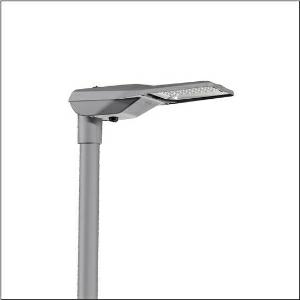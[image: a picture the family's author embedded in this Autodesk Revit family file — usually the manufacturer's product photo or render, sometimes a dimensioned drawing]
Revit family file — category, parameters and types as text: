
# Revit family: streetlight_sl_21_mini___p0_8ab_5xe2r33t08jb_257d
name_source: partatom
category: Lighting Fixtures
units: mm (PartAtom-declared; Revit-internal decimal feet)

## family parameters
Cut with Voids When Loaded = No
Host = Face
Light Source = No
Part Type = Normal
Room Calculation Point = No
Round Connector Dimension = Use Diameter
Shared = No

## types (1)
- --- (1 x LED, 11230 lm, 88.6 W, 3000K)
    Apparent Load = 89 VA
    CIE Flux Codes = 39 72 97 100 100
    Color Rendering = 70
    Color Temperature = 3000K
    Default Elevation = 1800 mm
    Description = Streetlight SL 21 mini, mast luminaire, primary light control with lens, of PMMA, primary optical cover: cover, of toughened safety glass, transparent, light distribution: P0.8aB, light emission: direct distribution, primary light characteristic: asymmetric, installation type: post-top, side-entry, LED, High Power LED, rated luminous flux: 11.230lm, luminous efficacy: 127lm/W, light colour: 730, colour temperature: 3000K, control gear: D4i, control: pre-setting: logarithmic dimming characteristic, flexible luminous flux parameterisation, time-dependent luminous flux control, constant luminous flux control, overheat protection, mains connection: 220..240V, AC, 50/60Hz, start of lifetime: 89W, end of service life: 92W, reduction: 41W, luminaire housing, of diecast aluminium, powder-coated, SITECO metallic grey (DB 702S), corrosivity category C5 high according to DIN EN ISO 12944, multi-level sealing system, sealing non-destructively replaceable, inclination adjustable: 0°, 5°, 10°, 15°, please order mast flange separately, length: 628mm, width: 235mm, height: 110mm, mast flange for spigot size: 42mm (side-entry): 5XC10008XM4, 60/48mm (side-entry/post-top): 5XC10108XM2, 76/60mm (side-entry/post-top): 5XC10108XM1, mounting height: 4..8m, Smart Interface below and above, protection rating (complete): IP66, insulation class (complete): insulation class II (safety insulation), certification: CE, ENEC, ENEC+, VDE, impact resistance: IK10, permissible operating ambient temperature for outdoor applications: -40..+50°C, standard-compliant lighting for roads and squares, packaging unit: 1 piece

Light Distribution: P0.8aB
    Height = 110 mm
    Lamp = 1 x LED
    Lamp Light Flux = 11230 lm
    Lamp Power = 88.6 W
    Lamp count = 1
    Length = 625 mm
    Luminous efficacy = 127 lm/W
    Manufacturer = Siteco
    ModVariant = No
    Model = 5XE2R33T08JB
    Number of Poles = 1
    OnlyDefault = Yes
    Power Factor = 1
    Product Name = Streetlight SL 21 mini | P0.8aB
    Product group = mast luminaire | pylon top
    ProductGroupID = 6100
    Protection Class = Protection class II
    Protection Degree = IP 66
    RLX_Detail_Level = 1
    RLX_Emergency_Light_Flux = 0 lm
    RLX_Emergency_Type = 0
    RLX_Emergency_Type_DB = No
    RlxData = <blob elided: 26073 chars, md5=24c0b75c>
    Socket = socket
    Standby Power = 0 W
    System Light Flux = 11230 lm
    System Power = 89 W
    Type Comments = factory setting: luminous flux: 100 % | dim-lin: 254 | 915 mA
    Type Image = l_1003514.jpg
    URL = http://relux.com
    VarID = @adj_032925
    Voltage = 0 V
    Weight = 0.00 kg
    Width = 234 mm

## geometry (parser evidence)
native form markers: Blend x4, Sweep x10
no freeform markers — native parametric forms only
